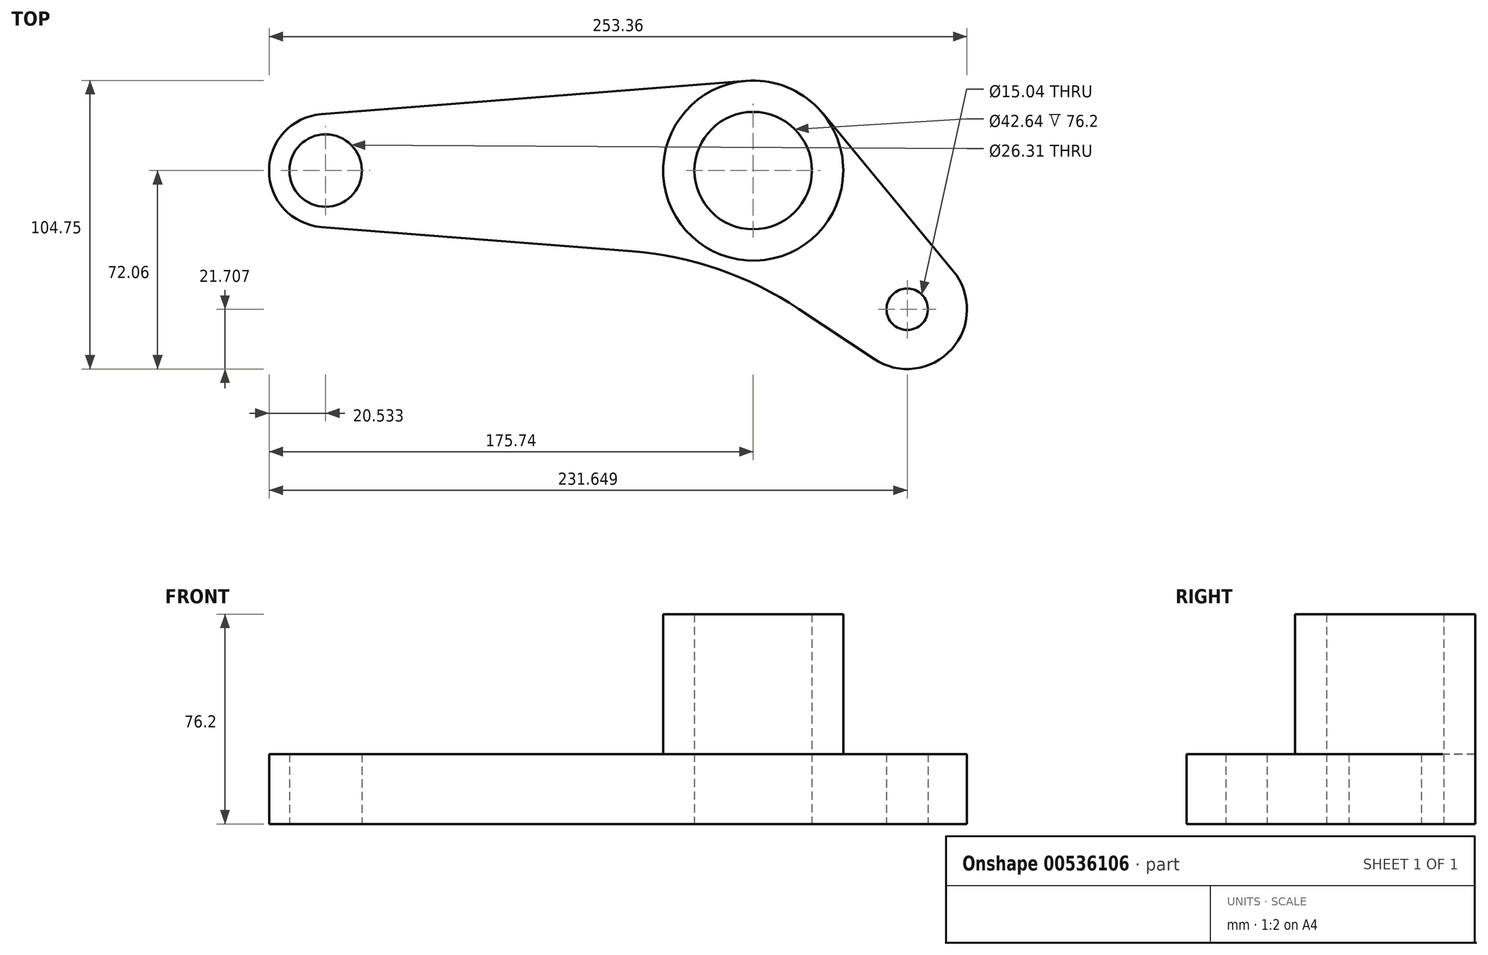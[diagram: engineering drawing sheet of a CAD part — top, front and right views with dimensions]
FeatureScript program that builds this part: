
annotation { "Feature Type Name" : "Feature", "Feature Type Description" : "" }
export const myFeature = defineFeature(function(context is Context, id is Id, definition is map)
    precondition{}
    {
        {
            var Q0;
            Q0=qCreatedBy(makeId("Top.planeOp"),FACE);
            var sketch = newSketch(context, id + "F0", { "sketchPlane" : qUnion([Q0])});
            skLineSegment(sketch, "E0", {"start": v(0, 0) * mm, "end": v(-155.2, 0) * mm, "construction": true});
            skLineSegment(sketch, "E1", {"start": v(0, 0) * mm, "end": v(55.9, -50.35) * mm, "construction": true});
            skCircle(sketch, "E2", {"center": v(-155.2, 0) * mm, "radius": 20.53 * mm});
            skCircle(sketch, "E3", {"center": v(-155.2, 0) * mm, "radius": 13.16 * mm});
            skCircle(sketch, "E4", {"center": v(0, 0) * mm, "radius": 32.69 * mm});
            skCircle(sketch, "E5", {"center": v(0, 0) * mm, "radius": 21.32 * mm});
            skCircle(sketch, "E6", {"center": v(55.9, -50.35) * mm, "radius": 7.52 * mm});
            skCircle(sketch, "E7", {"center": v(55.9, -50.35) * mm, "radius": 21.7 * mm});
            skLineSegment(sketch, "E8", {"start": v(-156.82, 20.47) * mm, "end": v(-2.56, 32.59) * mm});
            skLineSegment(sketch, "E9", {"start": v(25.18, 20.84) * mm, "end": v(72.64, -36.51) * mm});
            skLineSegment(sketch, "E10", {"start": v(-156.82, -20.47) * mm, "end": v(-43.92, -29.34) * mm});
            skLineSegment(sketch, "E11", {"start": v(43.89, -68.43) * mm, "end": v(16.45, -50.19) * mm});
            skPoint(sketch, "E12.visualSharp", {"position": v(-11.03, -31.92) * mm});
            skArc(sketch, "E12.filletArc", {"start": v(16.45, -50.19) * mm, "mid": v(-12.4, -35.9) * mm, "end": v(-43.92, -29.34) * mm});
            skSolve(sketch);
        }
        {
            var Q0;
            {var subQ3=sQuery(id+"F0.wireOp",EDGE,"E8");Q0=makeQuery(id+"F0.imprint","IMPRINT",FACE,{"disambiguationData":[TD([[makeQuery(id+"F0.imprint","IMPRINT",EDGE,{"derivedFrom":subQ3}),-1.0]])]});}
            var Q1;
            Q1=makeQuery(id+"F0.imprint","IMPRINT",FACE,{"disambiguationData":[TD([[makeQuery(id+"F0.imprint","IMPRINT",EDGE,{"derivedFrom":sQuery(id+"F0.wireOp",EDGE,"E3")}),-1.0]])]});
            var Q2;
            Q2=makeQuery(id+"F0.imprint","IMPRINT",FACE,{"disambiguationData":[TD([[makeQuery(id+"F0.imprint","IMPRINT",EDGE,{"derivedFrom":sQuery(id+"F0.wireOp",EDGE,"E6")}),-1.0]])]});
            var Q3;
            Q3=makeQuery(id+"F0.imprint","IMPRINT",FACE,{"disambiguationData":[TD([[makeQuery(id+"F0.imprint","IMPRINT",EDGE,{"derivedFrom":sQuery(id+"F0.wireOp",EDGE,"E5")}),-1.0]])]});
            extrude(context, id + "F1", {"entities" : qUnion([Q0, Q1, Q2, Q3]), "depth" : 25.4 * mm, "offsetDistance" : 25.4 * mm});
        }
        {
            var Q0;
            Q0=makeQuery(id+"F1.opExtrude","CAP_FACE",FACE,{"disambiguationData":[OSD([sQuery(id+"F0.wireOp",EDGE,"E2"),sQuery(id+"F0.wireOp",EDGE,"E3"),sQuery(id+"F0.wireOp",EDGE,"E4"),sQuery(id+"F0.wireOp",EDGE,"E5"),sQuery(id+"F0.wireOp",EDGE,"E6"),sQuery(id+"F0.wireOp",EDGE,"E7"),sQuery(id+"F0.wireOp",EDGE,"E8"),sQuery(id+"F0.wireOp",EDGE,"E9"),sQuery(id+"F0.wireOp",EDGE,"E10"),sQuery(id+"F0.wireOp",EDGE,"E11"),sQuery(id+"F0.wireOp",EDGE,"E12.filletArc")])],"isStart":false});
            var sketch = newSketch(context, id + "F2", { "sketchPlane" : qUnion([Q0])});
            skCircle(sketch, "E13", {"center": v(0, 0) * mm, "radius": 32.69 * mm});
            skCircle(sketch, "E14.0", {"center": v(0, 0) * mm, "radius": 21.32 * mm});
            skSolve(sketch);
        }
        {
            var Q0;
            Q0 = qSketchRegion(id + "F2", true);
            extrude(context, id + "F3", {"entities" : qUnion([Q0]), "operationType" : NewBodyOperationType.ADD, "depth" : 50.8 * mm, "offsetDistance" : 25.4 * mm});
        }
    });
